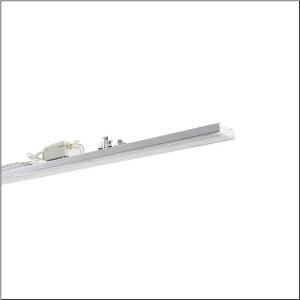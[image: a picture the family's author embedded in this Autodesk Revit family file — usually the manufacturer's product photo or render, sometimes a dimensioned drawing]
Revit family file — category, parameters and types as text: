
# Revit family: licross_r__21_recessed_mo_52tl11dn48xg_7dee
name_source: partatom
category: Lighting Fixtures
units: mm (PartAtom-declared; Revit-internal decimal feet)

## family parameters
Cut with Voids When Loaded = No
Host = Face
Light Source = No
Part Type = Normal
Room Calculation Point = No
Round Connector Dimension = Use Diameter
Shared = No

## types (1)
- --- (1 x LED, 8000 lm, 45 W, 4000K)
    Apparent Load = 45 VA
    CIE Flux Codes = 89 96 99 100 100
    Color Rendering = 80
    Color Temperature = 4000K
    Default Elevation = 1800 mm
    Description = Licross® 21 Recessed MO, luminaire insert, of sheet steel, galvanised, coil coated, white, length: 1.500mm, width: 66mm, height: 67mm, LED rated luminous flux: 8.000lm, light colour: 840, control gear: DALI 2, with plug, 5-pole, with phase selection, mains connection: 220..240V, AC, 50/60Hz, rated input power: 45W, halogen-free wiring, primary light control with lens, of plastic, primary optical cover: cover, of PMMA, light emission: direct distribution, primary light characteristic: symmetric, protection rating (complete): IP40, insulation class (complete): insulation class I (protective earthing), certification: CE, ENEC, VDE, UKCA, protection symbol: D if used in an environment without relevant dust loads with corresponding accessories, impact resistance: IK06, permissible ambient temperature for indoor applications: -25..+35°C, corresponds to IFS (International Featured Standards) requirements for safety and quality in the food industry, reducing of maximum allowable ambient temperature of 5°C with ceiling mounting, LABS conformity tested according to VDMA 24364:2018-05, packaging unit: 1 piece
    Height = 58 mm
    Lamp = 1 x LED
    Lamp Light Flux = 8000 lm
    Lamp Power = 45 W
    Lamp count = 1
    Length = 1500 mm
    Luminous efficacy = 178 lm/W
    Manufacturer = Siteco
    ModVariant = No
    Model = 52TL11DN48XG
    Mounting Place = Ceiling
    Mounting Type = Pendant
    Number of Poles = 1
    OnlyDefault = Yes
    Power Factor = 1
    Product Name = Licross® 21 Recessed MO
    Product group = luminaire insert
    ProductGroupID = 901
    Protection Class = Protection class I
    Protection Degree = IP 40
    RLX_Detail_Level = 1
    RLX_Emergency_Light_Flux = 0 lm
    RLX_Emergency_Type = 0
    RLX_Emergency_Type_DB = No
    RlxData = <blob elided: 24461 chars, md5=fcafdc02>
    Socket = socket
    Standby Power = 0 W
    System Light Flux = 8000 lm
    System Power = 45 W
    Type Comments = factory setting: luminous flux: 100 % | dim-lin: 254 | 302 mA
    Type Image = l_1296930.jpg
    URL = http://relux.com
    VarID = @adj_058459
    Voltage = 0 V
    Weight = 0.00 kg
    Width = 66 mm

## geometry (parser evidence)
native form markers: Blend x4, Sweep x13
no freeform markers — native parametric forms only
